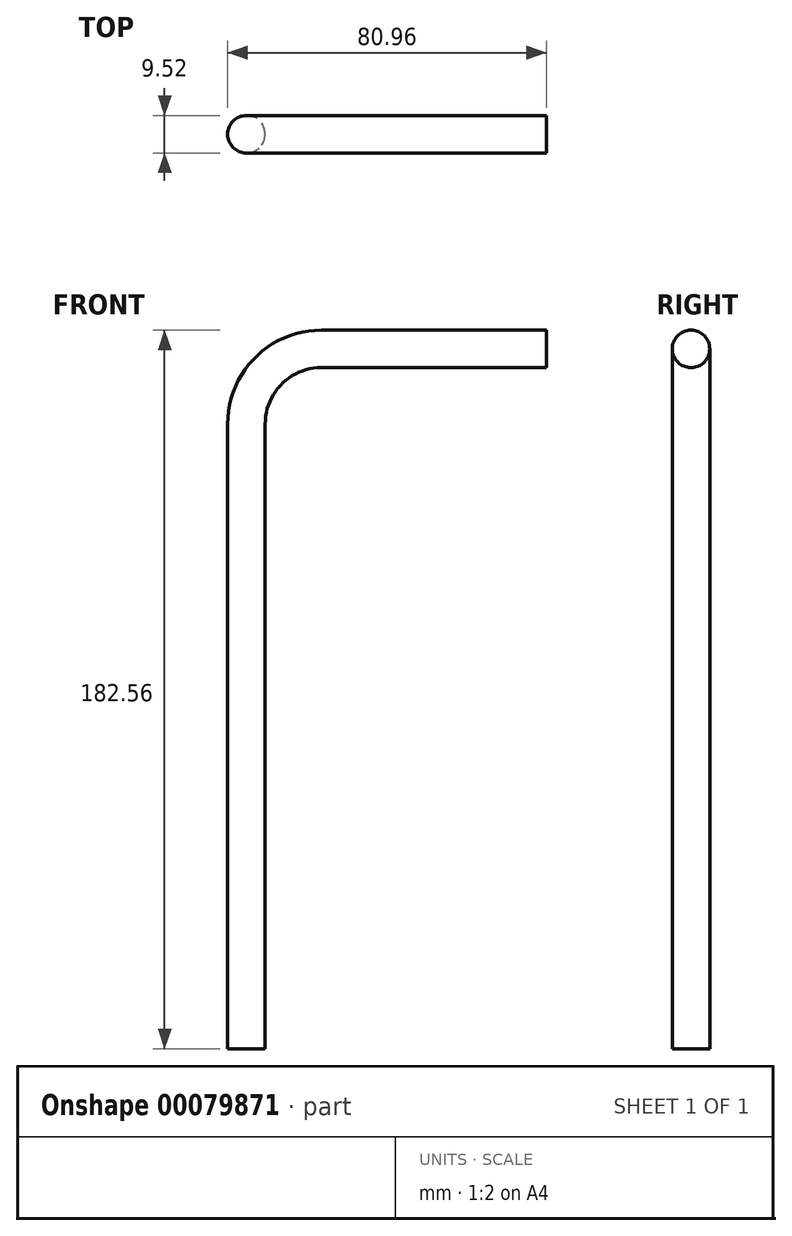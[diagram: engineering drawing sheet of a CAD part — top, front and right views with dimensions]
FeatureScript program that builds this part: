
annotation { "Feature Type Name" : "Feature", "Feature Type Description" : "" }
export const myFeature = defineFeature(function(context is Context, id is Id, definition is map)
    precondition{}
    {
        {
            var Q0;
            Q0=qCreatedBy(makeId("Front.planeOp"),FACE);
            var sketch = newSketch(context, id + "F0", { "sketchPlane" : qUnion([Q0])});
            skLineSegment(sketch, "E0", {"start": v(0, 0) * mm, "end": v(0, 158.75) * mm});
            skLineSegment(sketch, "E1", {"start": v(19.05, 177.8) * mm, "end": v(76.2, 177.8) * mm});
            skArc(sketch, "E2", {"start": v(19.05, 177.8) * mm, "mid": v(5.58, 172.22) * mm, "end": v(0, 158.75) * mm});
            skSolve(sketch);
        }
        {
            var Q0;
            Q0=qCreatedBy(makeId("Top.planeOp"),FACE);
            var sketch = newSketch(context, id + "F1", { "sketchPlane" : qUnion([Q0])});
            skCircle(sketch, "E3", {"center": v(0, 0) * mm, "radius": 4.76 * mm});
            skSolve(sketch);
        }
        {
            var Q0;
            Q0=sQuery(id+"F0.wireOp",VERTEX,"E1.end");
            var Q1;
            Q1=sQuery(id+"F0.wireOp",EDGE,"E1");
            cPlane(context, id + "F2", {"entities" : qUnion([Q0, Q1]), "cplaneType" : CPlaneType.LINE_POINT, "offset" : 152.4 * mm, "width" : 152.4 * mm, "height" : 152.4 * mm});
        }
        {
            var Q0;
            Q0=makeQuery(id+"F1.imprint","IMPRINT",FACE,{"disambiguationData":[TD([[makeQuery(id+"F1.imprint","IMPRINT",EDGE,{"derivedFrom":sQuery(id+"F1.wireOp",EDGE,"E3")}),1.0]])]});
            var Q1;
            Q1=sQuery(id+"F0.wireOp",EDGE,"E0");
            var Q2;
            Q2=sQuery(id+"F0.wireOp",EDGE,"E2");
            var Q3;
            Q3=sQuery(id+"F0.wireOp",EDGE,"E1");
            sweep(context, id + "F3", {"profiles" : qUnion([Q0]), "path" : qUnion([Q1, Q2, Q3])});
        }
    });
